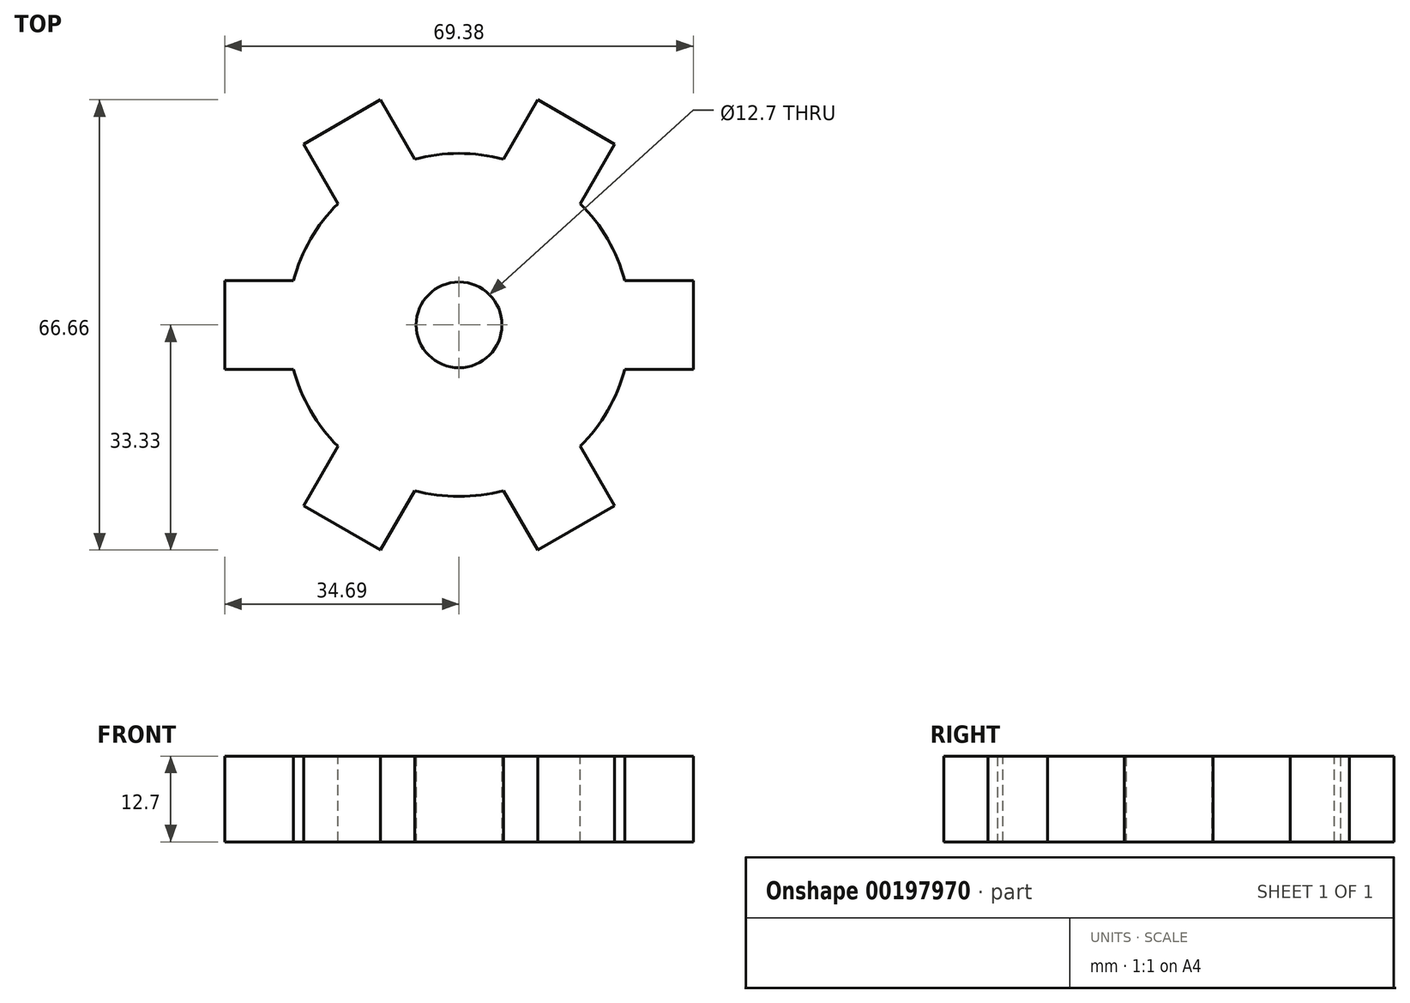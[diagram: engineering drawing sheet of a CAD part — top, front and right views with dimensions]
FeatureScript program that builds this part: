
annotation { "Feature Type Name" : "Feature", "Feature Type Description" : "" }
export const myFeature = defineFeature(function(context is Context, id is Id, definition is map)
    precondition{}
    {
        {
            var Q0;
            Q0=qCreatedBy(makeId("Top.planeOp"),FACE);
            var sketch = newSketch(context, id + "F0", { "sketchPlane" : qUnion([Q0])});
            skCircle(sketch, "E0", {"center": v(0, 0) * mm, "radius": 25.4 * mm});
            skSolve(sketch);
        }
        {
            var Q0;
            Q0 = qSketchRegion(id + "F0", true);
            extrude(context, id + "F1", {"entities" : qUnion([Q0]), "endBound" : BoundingType.SYMMETRIC, "depth" : 12.7 * mm});
        }
        {
            var Q0;
            Q0=makeQuery(id+"F1.opExtrude","CAP_FACE",FACE,{"disambiguationData":[OSD([sQuery(id+"F0.wireOp",EDGE,"E0")])],"isStart":false});
            var sketch = newSketch(context, id + "F2", { "sketchPlane" : qUnion([Q0])});
            skLineSegment(sketch, "E1", {"start": v(0, 0) * mm, "end": v(25.4, 0) * mm});
            skLineSegment(sketch, "E2", {"start": v(0, 0) * mm, "end": v(24.53, -6.57) * mm});
            skLineSegment(sketch, "E3", {"start": v(0, 0) * mm, "end": v(24.53, 6.57) * mm});
            skLineSegment(sketch, "E4", {"start": v(24.53, 6.57) * mm, "end": v(24.53, -6.57) * mm});
            skLineSegment(sketch, "E5.0", {"start": v(34.7, 6.57) * mm, "end": v(34.7, -6.57) * mm});
            skLineSegment(sketch, "E6", {"start": v(34.7, 6.57) * mm, "end": v(24.53, 6.57) * mm});
            skLineSegment(sketch, "E7", {"start": v(34.7, -6.57) * mm, "end": v(24.53, -6.57) * mm});
            skSolve(sketch);
        }
        {
            var Q0;
            Q0=makeQuery(id+"F2.imprint","IMPRINT",FACE,{"disambiguationData":[TD([[makeQuery(id+"F2.imprint","IMPRINT",EDGE,{"derivedFrom":sQuery(id+"F2.wireOp",EDGE,"E5.0")}),-1.0]])]});
            extrude(context, id + "F3", {"entities" : qUnion([Q0]), "operationType" : NewBodyOperationType.ADD, "oppositeDirection" : true, "depth" : 12.7 * mm});
        }
        {
            var Q0;
            Q0=qCreatedBy(makeId("Right.planeOp"),FACE);
            var sketch = newSketch(context, id + "F4", { "sketchPlane" : qUnion([Q0])});
            skLineSegment(sketch, "E8", {"start": v(0, 0) * mm, "end": v(0, -31.99) * mm});
            skSolve(sketch);
        }
        {
            var Q0;
            Q0=makeQuery(id+"F1.opExtrude","SWEPT_BODY",BODY,{"disambiguationData":[OSD([sQuery(id+"F0.wireOp",EDGE,"E0")])]});
            var Q1;
            Q1=sQuery(id+"F4.wireOp",EDGE,"E8");
            circularPattern(context, id + "F5", {"operationType" : NewBodyOperationType.ADD, "entities" : qUnion([Q0]), "axis" : qUnion([Q1]), "angle" : 360 * degree, "instanceCount" : 6, "equalSpace" : true});
        }
        {
            var Q0;
            {var subQ0=sQuery(id+"F0.wireOp",EDGE,"E0");var subQ1=makeQuery(id+"F3.boolean.opBoolean","MERGE",FACE,{"derivedFrom":[makeQuery(id+"F1.opExtrude","CAP_FACE",FACE,{"disambiguationData":[OSD([subQ0])],"isStart":true}),makeQuery(id+"F3.opExtrude","CAP_FACE",FACE,{"disambiguationData":[OSD([subQ0,sQuery(id+"F2.wireOp",EDGE,"E5.0"),sQuery(id+"F2.wireOp",EDGE,"E6"),sQuery(id+"F2.wireOp",EDGE,"E7")])],"isStart":false})]});Q0=makeQuery(id+"F5.boolean.opBoolean","MERGE",FACE,{"derivedFrom":[subQ1,makeQuery(id+"F5.opPattern","COPY",FACE,{"derivedFrom":subQ1,"instanceName":"1"}),makeQuery(id+"F5.opPattern","COPY",FACE,{"derivedFrom":subQ1,"instanceName":"2"}),makeQuery(id+"F5.opPattern","COPY",FACE,{"derivedFrom":subQ1,"instanceName":"3"}),makeQuery(id+"F5.opPattern","COPY",FACE,{"derivedFrom":subQ1,"instanceName":"4"}),makeQuery(id+"F5.opPattern","COPY",FACE,{"derivedFrom":subQ1,"instanceName":"5"})]});}
            var sketch = newSketch(context, id + "F6", { "sketchPlane" : qUnion([Q0])});
            skCircle(sketch, "E9", {"center": v(0, 0) * mm, "radius": 6.35 * mm});
            skSolve(sketch);
        }
        {
            var Q0;
            Q0 = qSketchRegion(id + "F6", true);
            extrude(context, id + "F7", {"entities" : qUnion([Q0]), "operationType" : NewBodyOperationType.REMOVE, "oppositeDirection" : true, "depth" : 25.4 * mm});
        }
    });
